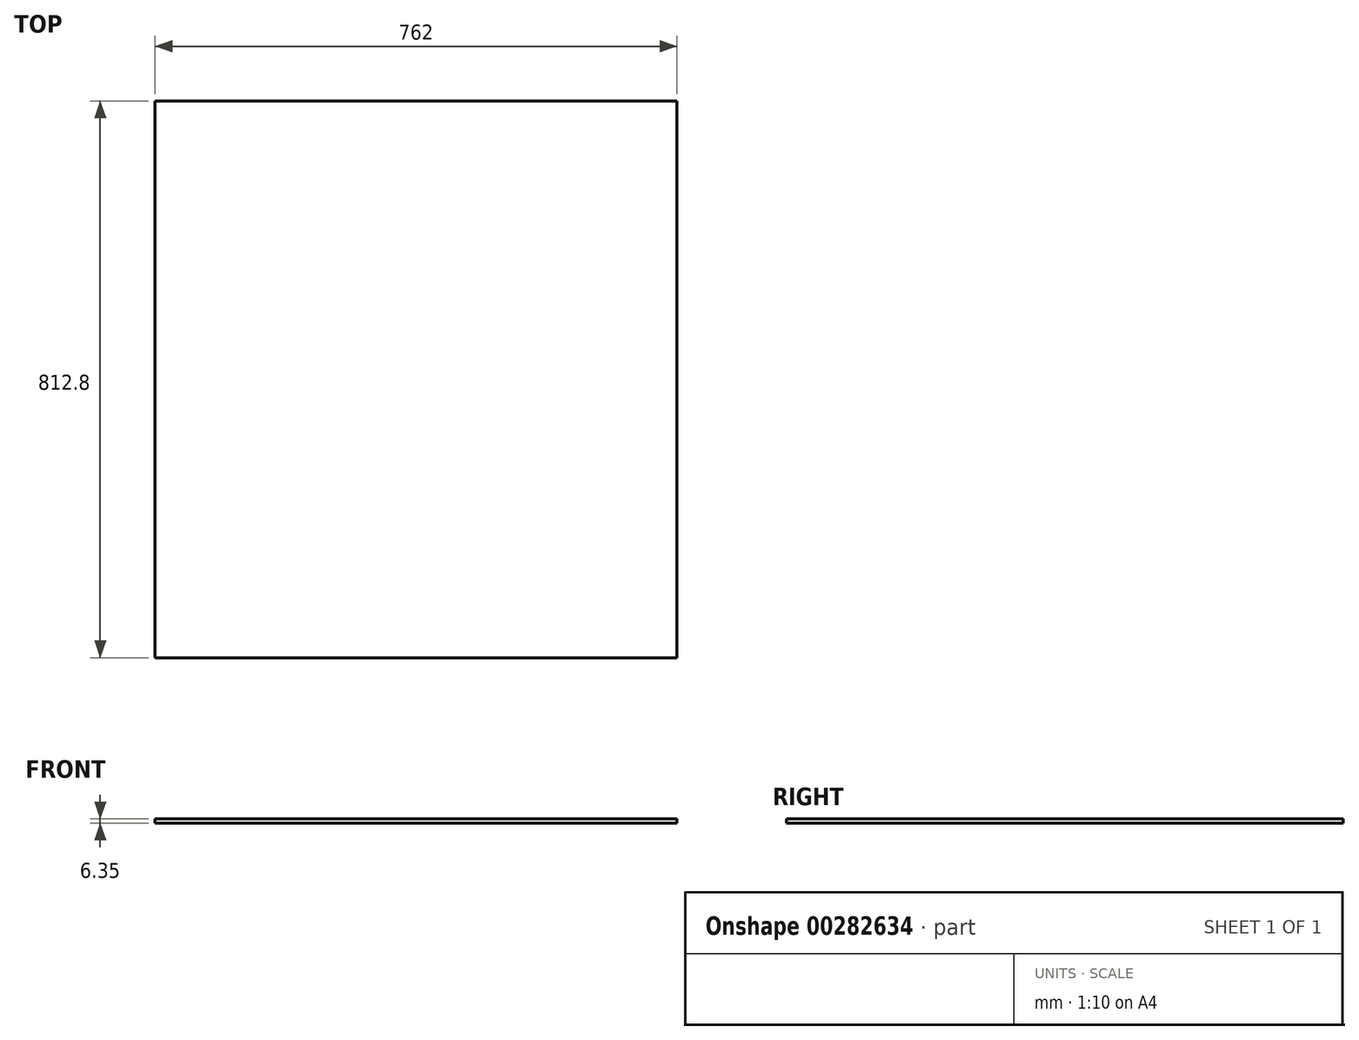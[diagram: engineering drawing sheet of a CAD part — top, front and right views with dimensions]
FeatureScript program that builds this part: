
annotation { "Feature Type Name" : "Feature", "Feature Type Description" : "" }
export const myFeature = defineFeature(function(context is Context, id is Id, definition is map)
    precondition{}
    {
        {
            var Q0;
            Q0=qCreatedBy(makeId("Top.planeOp"),FACE);
            var sketch = newSketch(context, id + "F0", { "sketchPlane" : qUnion([Q0])});
            skLineSegment(sketch, "E0.bottom", {"start": v(-586.12, 396.61) * mm, "end": v(175.88, 396.61) * mm});
            skLineSegment(sketch, "E0.top", {"start": v(-586.12, -416.19) * mm, "end": v(175.88, -416.19) * mm});
            skLineSegment(sketch, "E0.left", {"start": v(-586.12, 396.61) * mm, "end": v(-586.12, -416.19) * mm});
            skLineSegment(sketch, "E0.right", {"start": v(175.88, 396.61) * mm, "end": v(175.88, -416.19) * mm});
            skSolve(sketch);
        }
        {
            var Q0;
            Q0=makeQuery(id+"F0.imprint","IMPRINT",FACE,{"disambiguationData":[TD([[makeQuery(id+"F0.imprint","IMPRINT",EDGE,{"derivedFrom":sQuery(id+"F0.wireOp",EDGE,"E0.bottom")}),-1.0]])]});
            extrude(context, id + "F1", {"entities" : qUnion([Q0]), "depth" : 6.35 * mm});
        }
    });
